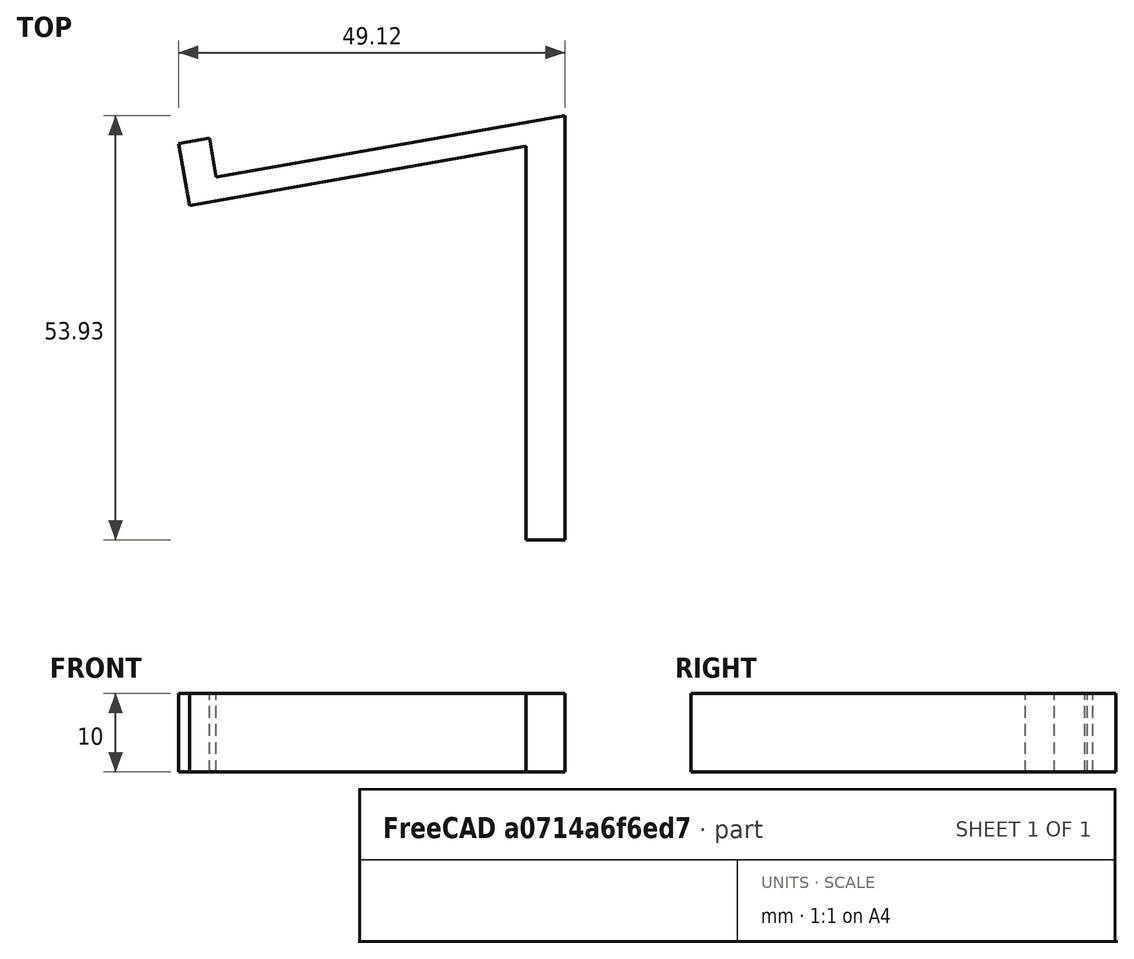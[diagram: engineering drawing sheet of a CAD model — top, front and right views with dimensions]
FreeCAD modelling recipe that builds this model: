
FCSTD DOCUMENT  (FreeCAD 0.16R)
Label: Hooks1
License: All rights reserved
LicenseURL: http://en.wikipedia.org/wiki/All_rights_reserved
objects: Sketcher::SketchObject×1, PartDesign::Pad×1, Mesh::Feature×1
note: 3 computed .brp shape members not serialized (recipe doc carries the construction recipe); baked Part::Feature solids carry a one-line shape summary decoded from their .brp

FEATURE [Sketcher::SketchObject] Sketch
  sketch-geometry (8):
    g0: LineSegment StartX=0 StartY=53.9279 StartZ=0 EndX=0 EndY=0 EndZ=0
    g1: LineSegment StartX=0 StartY=0 StartZ=0 EndX=-5 EndY=0 EndZ=0
    g2: LineSegment StartX=-5 StartY=0 StartZ=0 EndX=-5 EndY=50 EndZ=0
    g3: LineSegment StartX=-5 StartY=50 StartZ=0 EndX=-47.7346 EndY=42.4647 EndZ=0
    g4: LineSegment StartX=-47.7346 StartY=42.4647 StartZ=0 EndX=-49.1238 EndY=50.3432 EndZ=0
    g5: LineSegment StartX=-49.1238 StartY=50.3432 StartZ=0 EndX=-45.1846 EndY=51.0378 EndZ=0
    g6: LineSegment StartX=-45.1846 StartY=51.0378 StartZ=0 EndX=-44.3163 EndY=46.1137 EndZ=0
    g7: LineSegment StartX=-44.3163 StartY=46.1137 StartZ=0 EndX=0 EndY=53.9279 EndZ=0
  constraints (23):
    c: PointOnObject(g0,g-2)
    c: Coincident(g0,g-1)
    c: Coincident(g0,g1)
    c: PointOnObject(g1,g-1)
    c: Coincident(g1,g2)
    c: Vertical(g2)
    c: Coincident(g2,g3)
    c: Coincident(g3,g4)
    c: Coincident(g4,g5)
    c: Coincident(g5,g6)
    c: Coincident(g6,g7)
    c: Coincident(g7,g0)
    c: Angle(g3) = -2.96706
    c: Distance(g6) = 5
    c: Distance(g7) = 45
    c: Distance(g1) = 5
    c: Perpendicular(g4,g3)
    c: Parallel(g5,g3)
    c: Parallel(g6,g4)
    c: Distance(g5) = 4
    c: Distance(g6,g3) = 3
    c: Parallel(g7,g3)
    c: Distance(g2) = 50
FEATURE [PartDesign::Pad] Pad
  Length = 10
  Length2 = 100
  Sketch = -> Sketch
  Type = 0
FEATURE [Mesh::Feature] Mesh  label="Pad (Meshed)"
